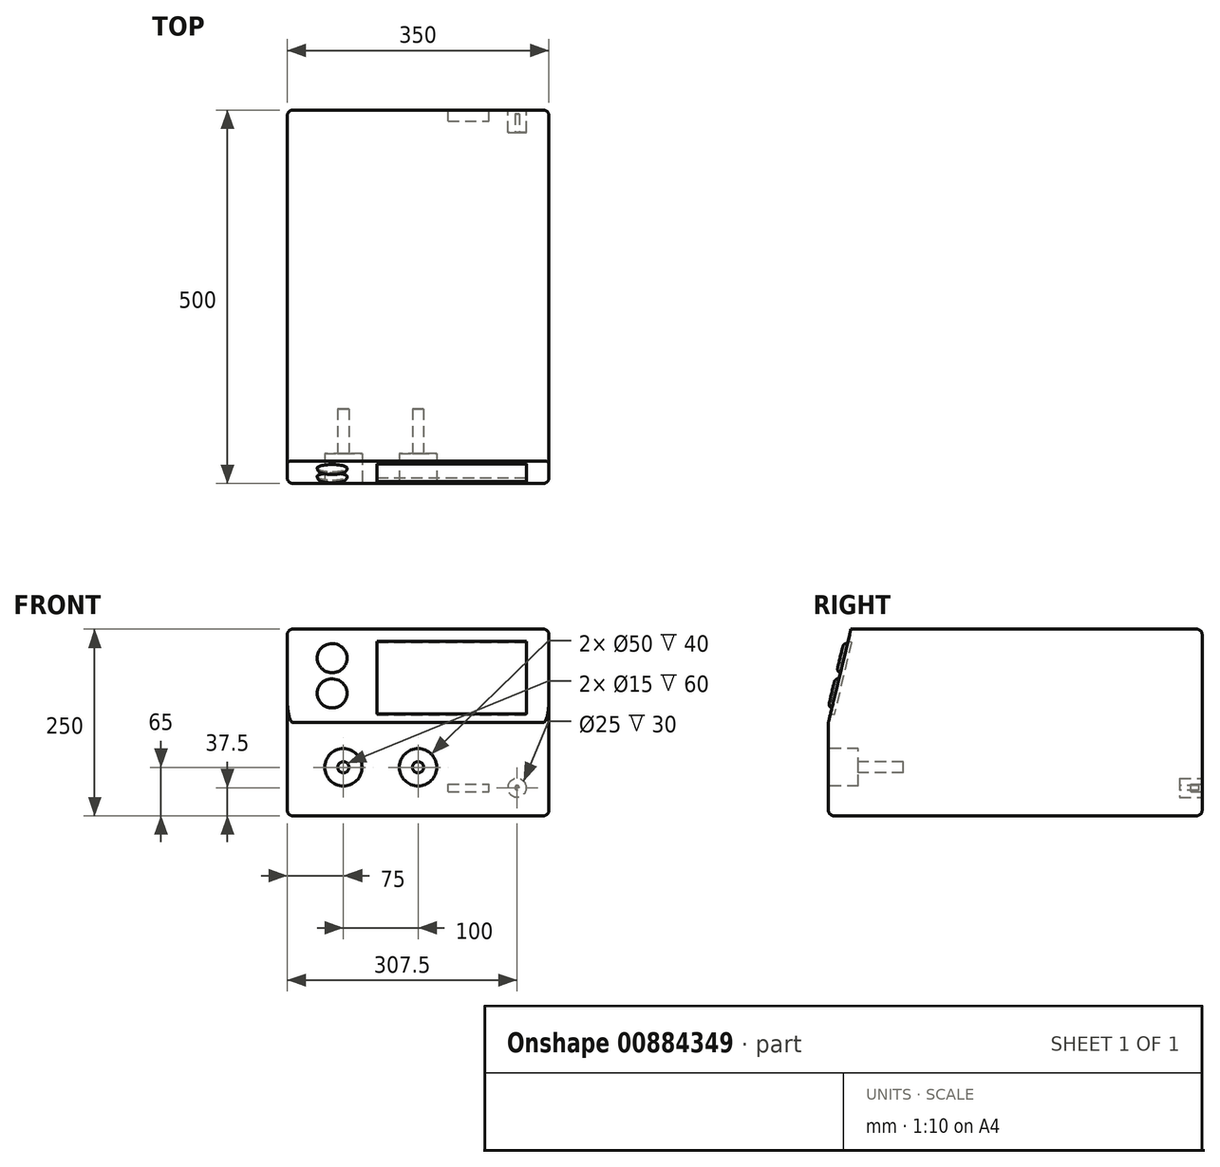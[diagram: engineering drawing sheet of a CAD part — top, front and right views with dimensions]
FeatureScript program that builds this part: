
annotation { "Feature Type Name" : "Feature", "Feature Type Description" : "" }
export const myFeature = defineFeature(function(context is Context, id is Id, definition is map)
    precondition{}
    {
        {
            var Q0;
            Q0=qCreatedBy(makeId("Top.planeOp"),FACE);
            var sketch = newSketch(context, id + "F0", { "sketchPlane" : qUnion([Q0])});
            skLineSegment(sketch, "E0.bottom", {"start": v(-175, 250) * mm, "end": v(175, 250) * mm});
            skLineSegment(sketch, "E0.top", {"start": v(-175, -250) * mm, "end": v(175, -250) * mm});
            skLineSegment(sketch, "E0.left", {"start": v(-175, 250) * mm, "end": v(-175, -250) * mm});
            skLineSegment(sketch, "E0.right", {"start": v(175, 250) * mm, "end": v(175, -250) * mm});
            skPoint(sketch, "E0.middle", {"position": v(0, 0) * mm});
            skSolve(sketch);
        }
        {
            var Q0;
            Q0 = qSketchRegion(id + "F0", true);
            extrude(context, id + "F1", {"entities" : qUnion([Q0]), "depth" : 250 * mm, "offsetDistance" : 25 * mm});
        }
        {
            var Q0;
            Q0=makeQuery(id+"F1.opExtrude","SWEPT_FACE",FACE,{"disambiguationData":[OSD([sQuery(id+"F0.wireOp",EDGE,"E0.right")])]});
            var sketch = newSketch(context, id + "F2", { "sketchPlane" : qUnion([Q0])});
            skLineSegment(sketch, "E1", {"start": v(-250, 250) * mm, "end": v(-250, 125) * mm});
            skLineSegment(sketch, "E2", {"start": v(-250, 125) * mm, "end": v(-220, 250) * mm});
            skLineSegment(sketch, "E3", {"start": v(-220, 250) * mm, "end": v(-250, 250) * mm});
            skSolve(sketch);
        }
        {
            var Q0;
            Q0 = qSketchRegion(id + "F2", true);
            extrude(context, id + "F3", {"entities" : qUnion([Q0]), "operationType" : NewBodyOperationType.REMOVE, "oppositeDirection" : true, "depth" : 350 * mm, "offsetDistance" : 25 * mm});
        }
        {
            var Q0;
            Q0=makeQuery(id+"F3.boolean.opBoolean","COPY",FACE,{"derivedFrom":makeQuery(id+"F3.opExtrude","SWEPT_FACE",FACE,{"disambiguationData":[OSD([sQuery(id+"F2.wireOp",EDGE,"E2")])]})});
            var sketch = newSketch(context, id + "F4", { "sketchPlane" : qUnion([Q0])});
            skCircle(sketch, "E4", {"center": v(-115, 151.75) * mm, "radius": 20 * mm});
            skSolve(sketch);
        }
        {
            var Q0;
            Q0 = qSketchRegion(id + "F4", true);
            extrude(context, id + "F5", {"entities" : qUnion([Q0]), "depth" : 5 * mm, "offsetDistance" : 25 * mm});
        }
        {
            var Q0;
            Q0=makeQuery(id+"F5.opExtrude","CAP_EDGE",EDGE,{"disambiguationData":[OSD([sQuery(id+"F4.wireOp",EDGE,"E4")])],"isStart":false});
            fillet(context, id + "F6", {"entities" : qUnion([Q0]), "radius" : 5 * mm, "tangentPropagation" : true, "allowEdgeOverflow" : false});
        }
        {
            var Q0;
            Q0=makeQuery(id+"F3.boolean.opBoolean","COPY",FACE,{"derivedFrom":makeQuery(id+"F3.opExtrude","SWEPT_FACE",FACE,{"disambiguationData":[OSD([sQuery(id+"F2.wireOp",EDGE,"E2")])]})});
            var sketch = newSketch(context, id + "F7", { "sketchPlane" : qUnion([Q0])});
            skCircle(sketch, "E5", {"center": v(-115, 103.2) * mm, "radius": 20 * mm});
            skSolve(sketch);
        }
        {
            var Q0;
            Q0 = qSketchRegion(id + "F7", true);
            extrude(context, id + "F8", {"entities" : qUnion([Q0]), "depth" : 5 * mm, "offsetDistance" : 25 * mm});
        }
        {
            var Q0;
            Q0=makeQuery(id+"F8.opExtrude","CAP_FACE",FACE,{"disambiguationData":[OSD([sQuery(id+"F7.wireOp",EDGE,"E5")])],"isStart":false});
            fillet(context, id + "F9", {"entities" : qUnion([Q0]), "radius" : 5 * mm, "tangentPropagation" : true, "allowEdgeOverflow" : false});
        }
        {
            var Q0;
            Q0=makeQuery(id+"F3.boolean.opBoolean","COPY",FACE,{"derivedFrom":makeQuery(id+"F3.opExtrude","SWEPT_FACE",FACE,{"disambiguationData":[OSD([sQuery(id+"F2.wireOp",EDGE,"E2")])]})});
            var sketch = newSketch(context, id + "F10", { "sketchPlane" : qUnion([Q0])});
            skLineSegment(sketch, "E6.bottom", {"start": v(-55, 174.75) * mm, "end": v(145, 174.75) * mm});
            skLineSegment(sketch, "E6.top", {"start": v(-55, 74.75) * mm, "end": v(145, 74.75) * mm});
            skLineSegment(sketch, "E6.left", {"start": v(-55, 174.75) * mm, "end": v(-55, 74.75) * mm});
            skLineSegment(sketch, "E6.right", {"start": v(145, 174.75) * mm, "end": v(145, 74.75) * mm});
            skSolve(sketch);
        }
        {
            var Q0;
            Q0=makeQuery(id+"F10.imprint","IMPRINT",FACE,{"disambiguationData":[TD([[makeQuery(id+"F10.imprint","IMPRINT",EDGE,{"derivedFrom":sQuery(id+"F10.wireOp",EDGE,"E6.bottom")}),-1.0]])]});
            extrude(context, id + "F11", {"entities" : qUnion([Q0]), "operationType" : NewBodyOperationType.REMOVE, "oppositeDirection" : true, "depth" : 5 * mm, "offsetDistance" : 25 * mm});
        }
        {
            var Q0;
            Q0=makeQuery(id+"F3.boolean.opBoolean","COPY",FACE,{"derivedFrom":makeQuery(id+"F3.opExtrude","SWEPT_FACE",FACE,{"disambiguationData":[OSD([sQuery(id+"F2.wireOp",EDGE,"E2")])]})});
            var sketch = newSketch(context, id + "F12", { "sketchPlane" : qUnion([Q0])});
            skLineSegment(sketch, "E7.bottom", {"start": v(-55, 174.75) * mm, "end": v(145, 174.75) * mm});
            skLineSegment(sketch, "E7.top", {"start": v(-55, 74.75) * mm, "end": v(145, 74.75) * mm});
            skLineSegment(sketch, "E7.left", {"start": v(-55, 174.75) * mm, "end": v(-55, 74.75) * mm});
            skLineSegment(sketch, "E7.right", {"start": v(145, 174.75) * mm, "end": v(145, 74.75) * mm});
            skSolve(sketch);
        }
        {
            var Q0;
            Q0 = qSketchRegion(id + "F12", true);
            extrude(context, id + "F13", {"entities" : qUnion([Q0]), "oppositeDirection" : true, "depth" : 5 * mm, "offsetDistance" : 25 * mm});
        }
        {
            var Q0;
            Q0=makeQuery(id+"F1.opExtrude","SWEPT_FACE",FACE,{"disambiguationData":[OSD([sQuery(id+"F0.wireOp",EDGE,"E0.top")])]});
            var sketch = newSketch(context, id + "F14", { "sketchPlane" : qUnion([Q0])});
            skCircle(sketch, "E8", {"center": v(0, 65) * mm, "radius": 25 * mm});
            skSolve(sketch);
        }
        {
            var Q0;
            Q0 = qSketchRegion(id + "F14", true);
            extrude(context, id + "F15", {"entities" : qUnion([Q0]), "operationType" : NewBodyOperationType.REMOVE, "oppositeDirection" : true, "depth" : 40 * mm, "offsetDistance" : 25 * mm});
        }
        {
            var Q0;
            Q0=makeQuery(id+"F15.boolean.opBoolean","COPY",FACE,{"derivedFrom":makeQuery(id+"F15.opExtrude","CAP_FACE",FACE,{"disambiguationData":[OSD([sQuery(id+"F14.wireOp",EDGE,"E8")])],"isStart":false})});
            var sketch = newSketch(context, id + "F16", { "sketchPlane" : qUnion([Q0])});
            skCircle(sketch, "E9", {"center": v(0, 65) * mm, "radius": 7.5 * mm});
            skSolve(sketch);
        }
        {
            var Q0;
            Q0 = qSketchRegion(id + "F16", true);
            extrude(context, id + "F17", {"entities" : qUnion([Q0]), "operationType" : NewBodyOperationType.REMOVE, "oppositeDirection" : true, "depth" : 60 * mm, "offsetDistance" : 25 * mm});
        }
        {
            var Q0;
            Q0=makeQuery(id+"F1.opExtrude","SWEPT_FACE",FACE,{"disambiguationData":[OSD([sQuery(id+"F0.wireOp",EDGE,"E0.top")])]});
            var sketch = newSketch(context, id + "F18", { "sketchPlane" : qUnion([Q0])});
            skCircle(sketch, "E10", {"center": v(-100, 65) * mm, "radius": 25 * mm});
            skSolve(sketch);
        }
        {
            var Q0;
            Q0 = qSketchRegion(id + "F18", true);
            extrude(context, id + "F19", {"entities" : qUnion([Q0]), "operationType" : NewBodyOperationType.REMOVE, "oppositeDirection" : true, "depth" : 40 * mm, "offsetDistance" : 25 * mm});
        }
        {
            var Q0;
            Q0=makeQuery(id+"F19.boolean.opBoolean","COPY",FACE,{"derivedFrom":makeQuery(id+"F19.opExtrude","CAP_FACE",FACE,{"disambiguationData":[OSD([sQuery(id+"F18.wireOp",EDGE,"E10")])],"isStart":false})});
            var sketch = newSketch(context, id + "F20", { "sketchPlane" : qUnion([Q0])});
            skCircle(sketch, "E11", {"center": v(-100, 65) * mm, "radius": 7.5 * mm});
            skSolve(sketch);
        }
        {
            var Q0;
            Q0 = qSketchRegion(id + "F20", true);
            extrude(context, id + "F21", {"entities" : qUnion([Q0]), "operationType" : NewBodyOperationType.REMOVE, "oppositeDirection" : true, "depth" : 60 * mm, "offsetDistance" : 25 * mm});
        }
        {
            var Q0;
            Q0=makeQuery(id+"F3.boolean.opBoolean","COPY",EDGE,{"derivedFrom":makeQuery(id+"F3.opExtrude","CAP_EDGE",EDGE,{"disambiguationData":[OSD([sQuery(id+"F2.wireOp",EDGE,"E2")])],"isStart":true})});
            var Q1;
            Q1=makeQuery(id+"F1.opExtrude","SWEPT_EDGE",EDGE,{"disambiguationData":[OSD([sQuery(id+"F0.wireOp",EDGE,"E0.top"),sQuery(id+"F0.wireOp",EDGE,"E0.right")])]});
            var Q2;
            Q2=makeQuery(id+"F3.boolean.opBoolean","COPY",EDGE,{"derivedFrom":makeQuery(id+"F3.opExtrude","SWEPT_EDGE",EDGE,{"disambiguationData":[OSD([sQuery(id+"F0.wireOp",EDGE,"E0.top"),sQuery(id+"F0.wireOp",EDGE,"E0.right"),sQuery(id+"F2.wireOp",EDGE,"E1"),sQuery(id+"F2.wireOp",EDGE,"E2")])]})});
            var Q3;
            Q3=makeQuery(id+"F1.opExtrude","CAP_EDGE",EDGE,{"disambiguationData":[OSD([sQuery(id+"F0.wireOp",EDGE,"E0.right")])],"isStart":false});
            var Q4;
            Q4=makeQuery(id+"F1.opExtrude","SWEPT_EDGE",EDGE,{"disambiguationData":[OSD([sQuery(id+"F0.wireOp",EDGE,"E0.bottom"),sQuery(id+"F0.wireOp",EDGE,"E0.right")])]});
            var Q5;
            Q5=makeQuery(id+"F1.opExtrude","CAP_EDGE",EDGE,{"disambiguationData":[OSD([sQuery(id+"F0.wireOp",EDGE,"E0.right")])],"isStart":true});
            var Q6;
            Q6=makeQuery(id+"F1.opExtrude","CAP_EDGE",EDGE,{"disambiguationData":[OSD([sQuery(id+"F0.wireOp",EDGE,"E0.top")])],"isStart":true});
            var Q7;
            Q7=makeQuery(id+"F1.opExtrude","SWEPT_EDGE",EDGE,{"disambiguationData":[OSD([sQuery(id+"F0.wireOp",EDGE,"E0.top"),sQuery(id+"F0.wireOp",EDGE,"E0.left")])]});
            var Q8;
            Q8=makeQuery(id+"F3.boolean.opBoolean","COPY",EDGE,{"derivedFrom":makeQuery(id+"F3.opExtrude","CAP_EDGE",EDGE,{"disambiguationData":[OSD([sQuery(id+"F2.wireOp",EDGE,"E2")])],"isStart":false})});
            var Q9;
            Q9=makeQuery(id+"F1.opExtrude","CAP_EDGE",EDGE,{"disambiguationData":[OSD([sQuery(id+"F0.wireOp",EDGE,"E0.left")])],"isStart":false});
            var Q10;
            Q10=makeQuery(id+"F1.opExtrude","SWEPT_EDGE",EDGE,{"disambiguationData":[OSD([sQuery(id+"F0.wireOp",EDGE,"E0.bottom"),sQuery(id+"F0.wireOp",EDGE,"E0.left")])]});
            var Q11;
            Q11=makeQuery(id+"F1.opExtrude","CAP_EDGE",EDGE,{"disambiguationData":[OSD([sQuery(id+"F0.wireOp",EDGE,"E0.left")])],"isStart":true});
            var Q12;
            Q12=makeQuery(id+"F1.opExtrude","CAP_EDGE",EDGE,{"disambiguationData":[OSD([sQuery(id+"F0.wireOp",EDGE,"E0.bottom")])],"isStart":true});
            var Q13;
            Q13=makeQuery(id+"F1.opExtrude","CAP_EDGE",EDGE,{"disambiguationData":[OSD([sQuery(id+"F0.wireOp",EDGE,"E0.bottom")])],"isStart":false});
            var Q14;
            Q14=makeQuery(id+"F3.boolean.opBoolean","COPY",EDGE,{"derivedFrom":makeQuery(id+"F3.opExtrude","SWEPT_EDGE",EDGE,{"disambiguationData":[OSD([sQuery(id+"F0.wireOp",EDGE,"E0.right"),sQuery(id+"F2.wireOp",EDGE,"E2"),sQuery(id+"F2.wireOp",EDGE,"E3")])]})});
            fillet(context, id + "F22", {"entities" : qUnion([Q0, Q1, Q2, Q3, Q4, Q5, Q6, Q7, Q8, Q9, Q10, Q11, Q12, Q13, Q14]), "radius" : 7.5 * mm, "tangentPropagation" : true, "allowEdgeOverflow" : false});
        }
        {
            var Q0;
            Q0=makeQuery(id+"F1.opExtrude","SWEPT_FACE",FACE,{"disambiguationData":[OSD([sQuery(id+"F0.wireOp",EDGE,"E0.bottom")])]});
            var sketch = newSketch(context, id + "F23", { "sketchPlane" : qUnion([Q0])});
            skCircle(sketch, "E12", {"center": v(-132.5, 37.5) * mm, "radius": 12.5 * mm});
            skSolve(sketch);
        }
        {
            var Q0;
            Q0 = qSketchRegion(id + "F23", true);
            extrude(context, id + "F24", {"entities" : qUnion([Q0]), "operationType" : NewBodyOperationType.REMOVE, "oppositeDirection" : true, "depth" : 30 * mm, "offsetDistance" : 25 * mm});
        }
        {
            var Q0;
            Q0=makeQuery(id+"F24.boolean.opBoolean","COPY",FACE,{"derivedFrom":makeQuery(id+"F24.opExtrude","CAP_FACE",FACE,{"disambiguationData":[OSD([sQuery(id+"F23.wireOp",EDGE,"E12")])],"isStart":false})});
            var sketch = newSketch(context, id + "F25", { "sketchPlane" : qUnion([Q0])});
            skCircle(sketch, "E13", {"center": v(-132.5, 37.5) * mm, "radius": 3 * mm});
            skSolve(sketch);
        }
        {
            var Q0;
            Q0 = qSketchRegion(id + "F25", true);
            extrude(context, id + "F26", {"entities" : qUnion([Q0]), "depth" : 25 * mm, "offsetDistance" : 25 * mm});
        }
        {
            var Q0;
            Q0=makeQuery(id+"F1.opExtrude","SWEPT_FACE",FACE,{"disambiguationData":[OSD([sQuery(id+"F0.wireOp",EDGE,"E0.bottom")])]});
            var sketch = newSketch(context, id + "F27", { "sketchPlane" : qUnion([Q0])});
            skLineSegment(sketch, "E14.bottom", {"start": v(-40, 32.5) * mm, "end": v(-95, 32.5) * mm});
            skLineSegment(sketch, "E14.top", {"start": v(-40, 42.5) * mm, "end": v(-95, 42.5) * mm});
            skLineSegment(sketch, "E14.left", {"start": v(-40, 32.5) * mm, "end": v(-40, 42.5) * mm});
            skLineSegment(sketch, "E14.right", {"start": v(-95, 32.5) * mm, "end": v(-95, 42.5) * mm});
            skPoint(sketch, "E14.middle", {"position": v(-67.5, 37.5) * mm});
            skSolve(sketch);
        }
        {
            var Q0;
            Q0 = qSketchRegion(id + "F27", true);
            extrude(context, id + "F28", {"entities" : qUnion([Q0]), "operationType" : NewBodyOperationType.REMOVE, "oppositeDirection" : true, "depth" : 15 * mm, "offsetDistance" : 25 * mm});
        }
    });
